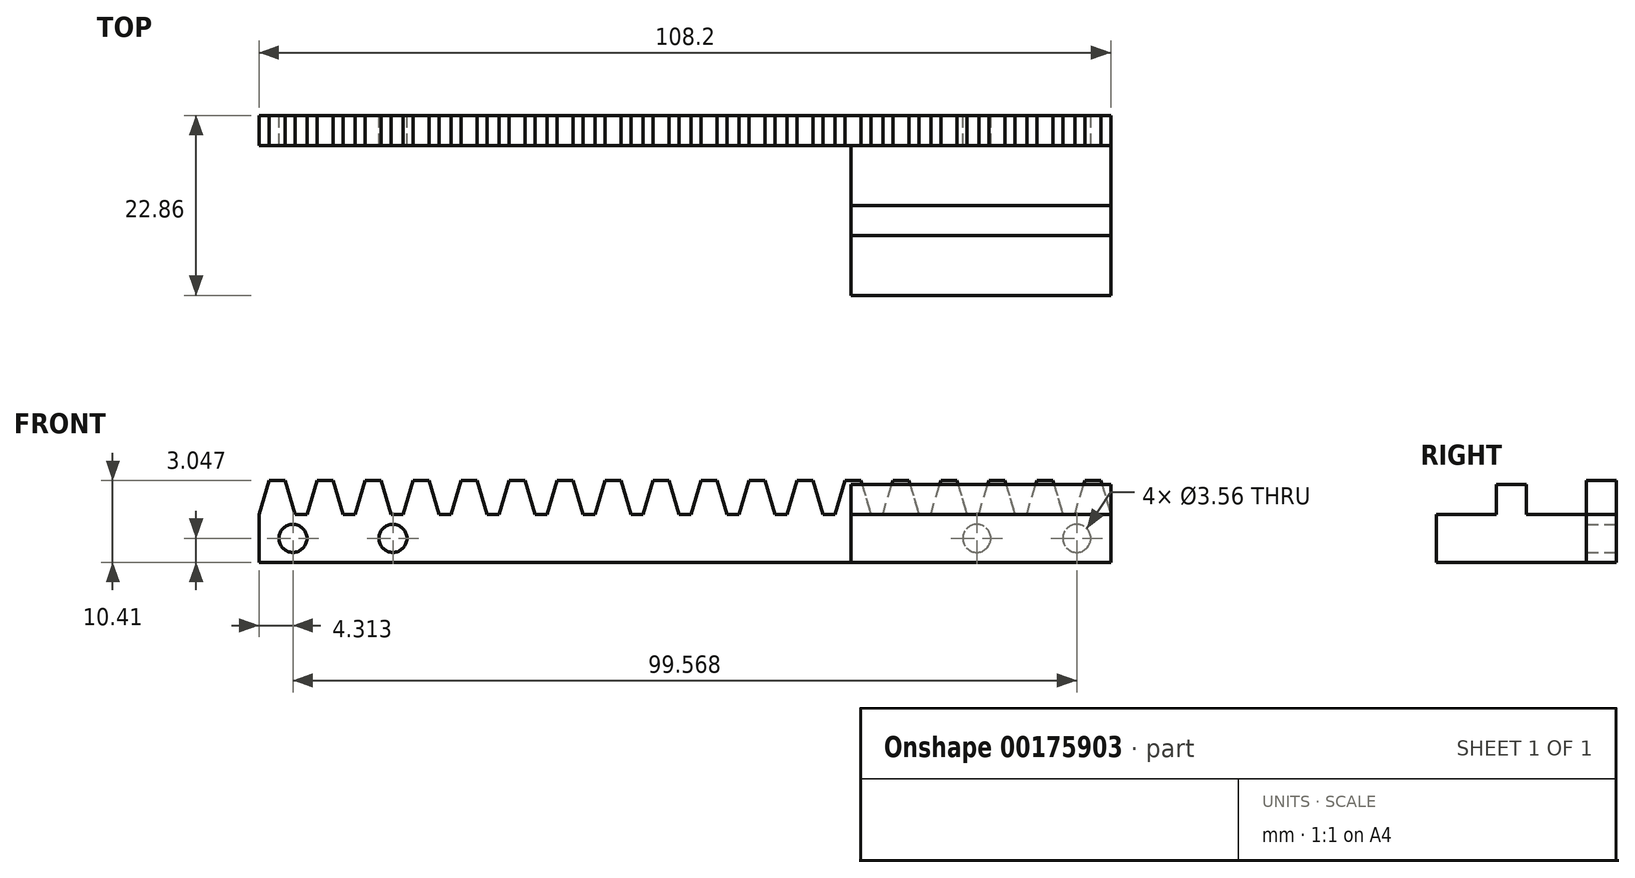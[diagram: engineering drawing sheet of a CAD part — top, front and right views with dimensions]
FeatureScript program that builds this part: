
annotation { "Feature Type Name" : "Feature", "Feature Type Description" : "" }
export const myFeature = defineFeature(function(context is Context, id is Id, definition is map)
    precondition{}
    {
        {
            var Q0;
            Q0=qCreatedBy(makeId("Front.planeOp"),FACE);
            var sketch = newSketch(context, id + "F0", { "sketchPlane" : qUnion([Q0])});
            skLineSegment(sketch, "E0.bottom", {"start": v(-38.44, 10.8) * mm, "end": v(69.76, 10.8) * mm});
            skLineSegment(sketch, "E0.top", {"start": v(-38.44, 16.9) * mm, "end": v(69.76, 16.9) * mm});
            skLineSegment(sketch, "E0.left", {"start": v(-38.44, 10.8) * mm, "end": v(-38.44, 16.9) * mm});
            skLineSegment(sketch, "E1", {"start": v(-38.44, 16.9) * mm, "end": v(-37.17, 21.21) * mm});
            skLineSegment(sketch, "E2", {"start": v(-37.17, 21.21) * mm, "end": v(-35.14, 21.21) * mm});
            skLineSegment(sketch, "E3", {"start": v(-35.14, 21.21) * mm, "end": v(-33.87, 16.9) * mm});
            skLineSegment(sketch, "E4", {"start": v(-38.44, 16.9) * mm, "end": v(-33.87, 16.9) * mm});
            skLineSegment(sketch, "E5", {"start": v(-36.16, 21.21) * mm, "end": v(-36.16, 16.9) * mm, "construction": true});
            skLineSegment(sketch, "E6", {"start": v(69.76, 10.8) * mm, "end": v(69.76, 16.9) * mm});
            skLineSegment(sketch, "E7.1.0.0", {"start": v(-29.05, 21.21) * mm, "end": v(-27.78, 16.9) * mm});
            skLineSegment(sketch, "E7.1.0.1", {"start": v(-32.35, 16.9) * mm, "end": v(-31.08, 21.21) * mm});
            skLineSegment(sketch, "E7.1.0.2", {"start": v(-31.08, 21.21) * mm, "end": v(-29.05, 21.21) * mm});
            skLineSegment(sketch, "E7.2.0.0", {"start": v(-22.95, 21.21) * mm, "end": v(-21.68, 16.9) * mm});
            skLineSegment(sketch, "E7.2.0.1", {"start": v(-26.25, 16.9) * mm, "end": v(-24.98, 21.21) * mm});
            skLineSegment(sketch, "E7.2.0.2", {"start": v(-24.98, 21.21) * mm, "end": v(-22.95, 21.21) * mm});
            skLineSegment(sketch, "E7.3.0.0", {"start": v(-16.85, 21.21) * mm, "end": v(-15.58, 16.9) * mm});
            skLineSegment(sketch, "E7.3.0.1", {"start": v(-20.16, 16.9) * mm, "end": v(-18.89, 21.21) * mm});
            skLineSegment(sketch, "E7.3.0.2", {"start": v(-18.89, 21.21) * mm, "end": v(-16.85, 21.21) * mm});
            skLineSegment(sketch, "E7.4.0.0", {"start": v(-10.76, 21.21) * mm, "end": v(-9.49, 16.9) * mm});
            skLineSegment(sketch, "E7.4.0.1", {"start": v(-14.06, 16.9) * mm, "end": v(-12.8, 21.21) * mm});
            skLineSegment(sketch, "E7.4.0.2", {"start": v(-12.8, 21.21) * mm, "end": v(-10.76, 21.21) * mm});
            skLineSegment(sketch, "E7.5.0.0", {"start": v(-4.66, 21.21) * mm, "end": v(-3.4, 16.9) * mm});
            skLineSegment(sketch, "E7.5.0.1", {"start": v(-7.96, 16.9) * mm, "end": v(-6.7, 21.21) * mm});
            skLineSegment(sketch, "E7.5.0.2", {"start": v(-6.7, 21.21) * mm, "end": v(-4.66, 21.21) * mm});
            skLineSegment(sketch, "E7.6.0.0", {"start": v(1.43, 21.21) * mm, "end": v(2.7, 16.9) * mm});
            skLineSegment(sketch, "E7.6.0.1", {"start": v(-1.87, 16.9) * mm, "end": v(-0.6, 21.21) * mm});
            skLineSegment(sketch, "E7.6.0.2", {"start": v(-0.6, 21.21) * mm, "end": v(1.43, 21.21) * mm});
            skLineSegment(sketch, "E7.7.0.0", {"start": v(7.53, 21.21) * mm, "end": v(8.8, 16.9) * mm});
            skLineSegment(sketch, "E7.7.0.1", {"start": v(4.23, 16.9) * mm, "end": v(5.5, 21.21) * mm});
            skLineSegment(sketch, "E7.7.0.2", {"start": v(5.5, 21.21) * mm, "end": v(7.53, 21.21) * mm});
            skLineSegment(sketch, "E7.8.0.0", {"start": v(13.63, 21.21) * mm, "end": v(14.9, 16.9) * mm});
            skLineSegment(sketch, "E7.8.0.1", {"start": v(10.32, 16.9) * mm, "end": v(11.6, 21.21) * mm});
            skLineSegment(sketch, "E7.8.0.2", {"start": v(11.6, 21.21) * mm, "end": v(13.63, 21.21) * mm});
            skLineSegment(sketch, "E7.9.0.0", {"start": v(19.72, 21.21) * mm, "end": v(21, 16.9) * mm});
            skLineSegment(sketch, "E7.9.0.1", {"start": v(16.42, 16.9) * mm, "end": v(17.69, 21.21) * mm});
            skLineSegment(sketch, "E7.9.0.2", {"start": v(17.69, 21.21) * mm, "end": v(19.72, 21.21) * mm});
            skLineSegment(sketch, "E7.10.0.0", {"start": v(25.82, 21.21) * mm, "end": v(27.09, 16.9) * mm});
            skLineSegment(sketch, "E7.10.0.1", {"start": v(22.52, 16.9) * mm, "end": v(23.79, 21.21) * mm});
            skLineSegment(sketch, "E7.10.0.2", {"start": v(23.79, 21.21) * mm, "end": v(25.82, 21.21) * mm});
            skLineSegment(sketch, "E7.11.0.0", {"start": v(31.91, 21.21) * mm, "end": v(33.18, 16.9) * mm});
            skLineSegment(sketch, "E7.11.0.1", {"start": v(28.61, 16.9) * mm, "end": v(29.88, 21.21) * mm});
            skLineSegment(sketch, "E7.11.0.2", {"start": v(29.88, 21.21) * mm, "end": v(31.91, 21.21) * mm});
            skLineSegment(sketch, "E7.12.0.0", {"start": v(38, 21.21) * mm, "end": v(39.28, 16.9) * mm});
            skLineSegment(sketch, "E7.12.0.1", {"start": v(34.7, 16.9) * mm, "end": v(35.98, 21.21) * mm});
            skLineSegment(sketch, "E7.12.0.2", {"start": v(35.98, 21.21) * mm, "end": v(38, 21.21) * mm});
            skLineSegment(sketch, "E7.13.0.0", {"start": v(44.1, 21.21) * mm, "end": v(45.38, 16.9) * mm});
            skLineSegment(sketch, "E7.13.0.1", {"start": v(40.8, 16.9) * mm, "end": v(42.07, 21.21) * mm});
            skLineSegment(sketch, "E7.13.0.2", {"start": v(42.07, 21.21) * mm, "end": v(44.1, 21.21) * mm});
            skLineSegment(sketch, "E7.14.0.0", {"start": v(50.2, 21.21) * mm, "end": v(51.47, 16.9) * mm});
            skLineSegment(sketch, "E7.14.0.1", {"start": v(46.9, 16.9) * mm, "end": v(48.17, 21.21) * mm});
            skLineSegment(sketch, "E7.14.0.2", {"start": v(48.17, 21.21) * mm, "end": v(50.2, 21.21) * mm});
            skLineSegment(sketch, "E7.15.0.0", {"start": v(56.3, 21.21) * mm, "end": v(57.57, 16.9) * mm});
            skLineSegment(sketch, "E7.15.0.1", {"start": v(53, 16.9) * mm, "end": v(54.27, 21.21) * mm});
            skLineSegment(sketch, "E7.15.0.2", {"start": v(54.27, 21.21) * mm, "end": v(56.3, 21.21) * mm});
            skLineSegment(sketch, "E7.16.0.0", {"start": v(62.4, 21.21) * mm, "end": v(63.66, 16.9) * mm});
            skLineSegment(sketch, "E7.16.0.1", {"start": v(59.1, 16.9) * mm, "end": v(60.36, 21.21) * mm});
            skLineSegment(sketch, "E7.16.0.2", {"start": v(60.36, 21.21) * mm, "end": v(62.4, 21.21) * mm});
            skLineSegment(sketch, "E7.17.0.0", {"start": v(68.49, 21.21) * mm, "end": v(69.76, 16.9) * mm});
            skLineSegment(sketch, "E7.17.0.1", {"start": v(65.19, 16.9) * mm, "end": v(66.46, 21.21) * mm});
            skLineSegment(sketch, "E7.17.0.2", {"start": v(66.46, 21.21) * mm, "end": v(68.49, 21.21) * mm});
            skLineSegment(sketch, "E7.direction1", {"start": v(-38.44, 16.9) * mm, "end": v(-32.35, 16.9) * mm, "construction": true});
            skPoint(sketch, "E8.centerSnap0", {"position": v(-38.44, 13.85) * mm});
            skSolve(sketch);
        }
        {
            var Q0;
            Q0=qSketchRegion(id+"F0",true);
            extrude(context, id + "F1", {"entities" : qUnion([Q0]), "depth" : 3.8 * mm});
        }
        {
            var Q0;
            Q0=makeQuery(id+"F1.opExtrude","CAP_FACE",FACE,{"disambiguationData":[OSD([sQuery(id+"F0.wireOp",EDGE,"E0.bottom"),sQuery(id+"F0.wireOp",EDGE,"E0.top"),sQuery(id+"F0.wireOp",EDGE,"E0.left"),sQuery(id+"F0.wireOp",EDGE,"E1"),sQuery(id+"F0.wireOp",EDGE,"E2"),sQuery(id+"F0.wireOp",EDGE,"E3"),sQuery(id+"F0.wireOp",EDGE,"E6"),sQuery(id+"F0.wireOp",EDGE,"E7.1.0.0"),sQuery(id+"F0.wireOp",EDGE,"E7.1.0.1"),sQuery(id+"F0.wireOp",EDGE,"E7.1.0.2"),sQuery(id+"F0.wireOp",EDGE,"E7.2.0.0"),sQuery(id+"F0.wireOp",EDGE,"E7.2.0.1"),sQuery(id+"F0.wireOp",EDGE,"E7.2.0.2"),sQuery(id+"F0.wireOp",EDGE,"E7.3.0.0"),sQuery(id+"F0.wireOp",EDGE,"E7.3.0.1"),sQuery(id+"F0.wireOp",EDGE,"E7.3.0.2"),sQuery(id+"F0.wireOp",EDGE,"E7.4.0.0"),sQuery(id+"F0.wireOp",EDGE,"E7.4.0.1"),sQuery(id+"F0.wireOp",EDGE,"E7.4.0.2"),sQuery(id+"F0.wireOp",EDGE,"E7.5.0.0"),sQuery(id+"F0.wireOp",EDGE,"E7.5.0.1"),sQuery(id+"F0.wireOp",EDGE,"E7.5.0.2"),sQuery(id+"F0.wireOp",EDGE,"E7.6.0.0"),sQuery(id+"F0.wireOp",EDGE,"E7.6.0.1"),sQuery(id+"F0.wireOp",EDGE,"E7.6.0.2"),sQuery(id+"F0.wireOp",EDGE,"E7.7.0.0"),sQuery(id+"F0.wireOp",EDGE,"E7.7.0.1"),sQuery(id+"F0.wireOp",EDGE,"E7.7.0.2"),sQuery(id+"F0.wireOp",EDGE,"E7.8.0.0"),sQuery(id+"F0.wireOp",EDGE,"E7.8.0.1"),sQuery(id+"F0.wireOp",EDGE,"E7.8.0.2"),sQuery(id+"F0.wireOp",EDGE,"E7.9.0.0"),sQuery(id+"F0.wireOp",EDGE,"E7.9.0.1"),sQuery(id+"F0.wireOp",EDGE,"E7.9.0.2"),sQuery(id+"F0.wireOp",EDGE,"E7.10.0.0"),sQuery(id+"F0.wireOp",EDGE,"E7.10.0.1"),sQuery(id+"F0.wireOp",EDGE,"E7.10.0.2"),sQuery(id+"F0.wireOp",EDGE,"E7.11.0.0"),sQuery(id+"F0.wireOp",EDGE,"E7.11.0.1"),sQuery(id+"F0.wireOp",EDGE,"E7.11.0.2"),sQuery(id+"F0.wireOp",EDGE,"E7.12.0.0"),sQuery(id+"F0.wireOp",EDGE,"E7.12.0.1"),sQuery(id+"F0.wireOp",EDGE,"E7.12.0.2"),sQuery(id+"F0.wireOp",EDGE,"E7.13.0.0"),sQuery(id+"F0.wireOp",EDGE,"E7.13.0.1"),sQuery(id+"F0.wireOp",EDGE,"E7.13.0.2"),sQuery(id+"F0.wireOp",EDGE,"E7.14.0.0"),sQuery(id+"F0.wireOp",EDGE,"E7.14.0.1"),sQuery(id+"F0.wireOp",EDGE,"E7.14.0.2"),sQuery(id+"F0.wireOp",EDGE,"E7.15.0.0"),sQuery(id+"F0.wireOp",EDGE,"E7.15.0.1"),sQuery(id+"F0.wireOp",EDGE,"E7.15.0.2"),sQuery(id+"F0.wireOp",EDGE,"E7.16.0.0"),sQuery(id+"F0.wireOp",EDGE,"E7.16.0.1"),sQuery(id+"F0.wireOp",EDGE,"E7.16.0.2"),sQuery(id+"F0.wireOp",EDGE,"E7.17.0.0"),sQuery(id+"F0.wireOp",EDGE,"E7.17.0.1"),sQuery(id+"F0.wireOp",EDGE,"E7.17.0.2")])],"isStart":true});
            var sketch = newSketch(context, id + "F2", { "sketchPlane" : qUnion([Q0])});
            skCircle(sketch, "E9", {"center": v(-52.74, 13.85) * mm, "radius": 1.78 * mm});
            skCircle(sketch, "E10", {"center": v(-65.44, 13.85) * mm, "radius": 1.78 * mm});
            skLineSegment(sketch, "E11", {"start": v(-65.19, 16.9) * mm, "end": v(-69.76, 16.9) * mm, "construction": true});
            skCircle(sketch, "E12", {"center": v(21.43, 13.85) * mm, "radius": 1.78 * mm});
            skCircle(sketch, "E13", {"center": v(34.13, 13.85) * mm, "radius": 1.78 * mm});
            skSolve(sketch);
        }
        {
            var Q0;
            Q0=qSketchRegion(id+"F2",true);
            extrude(context, id + "F3", {"entities" : qUnion([Q0]), "operationType" : NewBodyOperationType.REMOVE, "endBound" : BoundingType.UP_TO_NEXT, "oppositeDirection" : true, "depth" : 25.4 * mm});
        }
        {
            var Q0;
            Q0=qCreatedBy(makeId("Right.planeOp"),FACE);
            var Q1;
            Q1=makeQuery(id+"F1.opExtrude","CAP_VERTEX",VERTEX,{"disambiguationData":[OSD([sQuery(id+"F0.wireOp",EDGE,"E0.bottom"),sQuery(id+"F0.wireOp",EDGE,"E6")])],"isStart":false});
            cPlane(context, id + "F4", {"entities" : qUnion([Q0, Q1]), "cplaneType" : CPlaneType.PLANE_POINT, "offset" : 25.4 * mm, "width" : 152.4 * mm, "height" : 152.4 * mm});
        }
        {
            var Q0;
            Q0=qCreatedBy(id+"F4.planeOp",FACE);
            var sketch = newSketch(context, id + "F5", { "sketchPlane" : qUnion([Q0])});
            skLineSegment(sketch, "E14.0", {"start": v(-3.81, 10.8) * mm, "end": v(-3.81, 16.9) * mm});
            skLineSegment(sketch, "E15", {"start": v(-22.86, 16.9) * mm, "end": v(-15.24, 16.9) * mm});
            skLineSegment(sketch, "E16", {"start": v(-11.43, 16.9) * mm, "end": v(-11.43, 20.7) * mm});
            skLineSegment(sketch, "E17", {"start": v(-11.43, 20.7) * mm, "end": v(-15.24, 20.7) * mm});
            skLineSegment(sketch, "E18", {"start": v(-15.24, 20.7) * mm, "end": v(-15.24, 16.9) * mm});
            skLineSegment(sketch, "E19.trimOffspring", {"start": v(-11.43, 16.9) * mm, "end": v(-3.81, 16.9) * mm});
            skLineSegment(sketch, "E20", {"start": v(-3.81, 10.8) * mm, "end": v(-22.86, 10.8) * mm});
            skLineSegment(sketch, "E21", {"start": v(-22.86, 10.8) * mm, "end": v(-22.86, 16.9) * mm});
            skSolve(sketch);
        }
        {
            var Q0;
            Q0=qSketchRegion(id+"F5",true);
            extrude(context, id + "F6", {"entities" : qUnion([Q0]), "oppositeDirection" : true, "depth" : 33.02 * mm});
        }
    });
